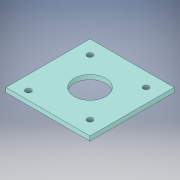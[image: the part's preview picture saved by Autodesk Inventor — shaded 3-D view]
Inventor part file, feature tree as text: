
AUTODESK INVENTOR PART (.ipt)
format: ipt  version: 2019 (Build 230136000, 136)  size: 131,072 bytes
history: native  units: mm
features: other x1, extrude x1, sketch x1
ambient origin geometry x8: Origin, YZ Plane, XZ Plane, XY Plane, X Axis, Y Axis, Z Axis, Center Point
bodies: Body1 (feature_tree)
feature tree (3):
  other  "Sólido1"
  extrude  "Extrusión1"  Depth=60.0mm
  sketch  "Boceto1"  dims[d0=22.6mm d1=60.0mm d2=60.0mm d3=4.0mm d4=4.0mm d5=4.0mm d6=4.0mm d7=40.0mm d8=20.0mm d9=20.0mm d10=40.0mm d11=40.0mm d12=20.0mm d13=40.0mm d14=20.0mm d15=3.18mm d16=0.0mm]
